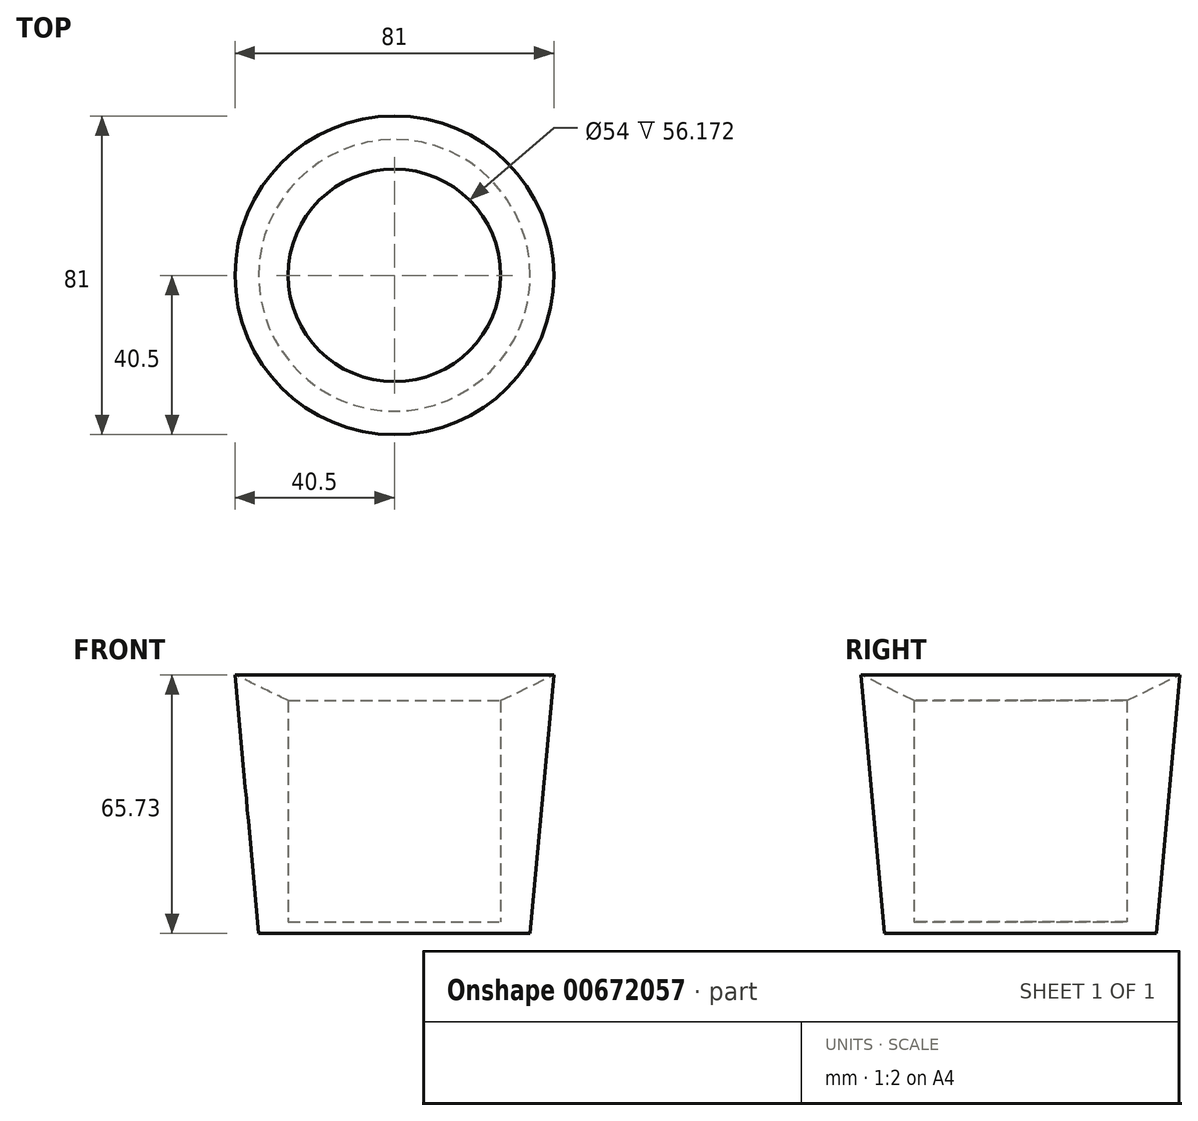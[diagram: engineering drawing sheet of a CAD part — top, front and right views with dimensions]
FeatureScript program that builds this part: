
annotation { "Feature Type Name" : "Feature", "Feature Type Description" : "" }
export const myFeature = defineFeature(function(context is Context, id is Id, definition is map)
    precondition{}
    {
        {
            var Q0;
            Q0=qCreatedBy(makeId("Right.planeOp"),FACE);
            var sketch = newSketch(context, id + "F0", { "sketchPlane" : qUnion([Q0])});
            skLineSegment(sketch, "E0", {"start": v(-40.5, 65.73) * mm, "end": v(-34.5, 0) * mm});
            skLineSegment(sketch, "E1", {"start": v(-34.5, 0) * mm, "end": v(0, 0) * mm});
            skLineSegment(sketch, "E2", {"start": v(0, 0) * mm, "end": v(0, 3) * mm});
            skLineSegment(sketch, "E3", {"start": v(0, 3) * mm, "end": v(-27, 3) * mm});
            skLineSegment(sketch, "E4", {"start": v(-27, 3) * mm, "end": v(-27, 59.17) * mm});
            skLineSegment(sketch, "E5", {"start": v(-27, 59.17) * mm, "end": v(-40.5, 65.73) * mm});
            skSolve(sketch);
        }
        {
            var Q0;
            Q0=makeQuery(id+"F0.imprint","IMPRINT",FACE,{"disambiguationData":[TD([[makeQuery(id+"F0.imprint","IMPRINT",EDGE,{"derivedFrom":sQuery(id+"F0.wireOp",EDGE,"E0")}),1.0]])]});
            var Q1;
            Q1=sQuery(id+"F0.wireOp",EDGE,"E2");
            revolve(context, id + "F1", {"entities" : qUnion([Q0]), "axis" : qUnion([Q1]), "revolveType" : RevolveType.FULL});
        }
    });
